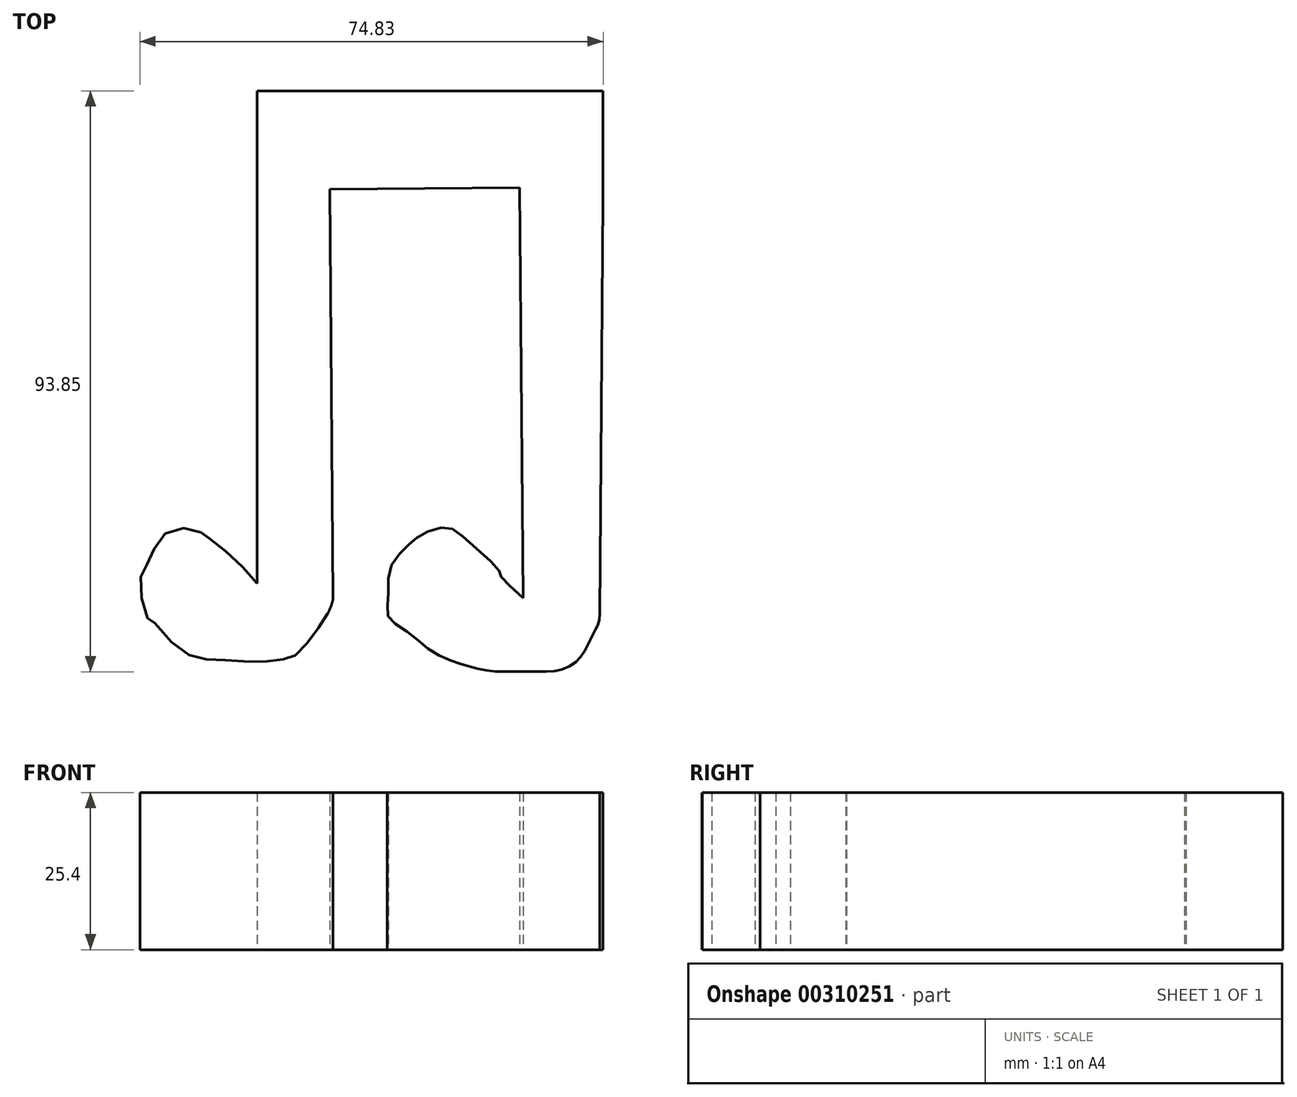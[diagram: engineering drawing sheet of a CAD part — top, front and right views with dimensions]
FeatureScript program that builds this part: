
annotation { "Feature Type Name" : "Feature", "Feature Type Description" : "" }
export const myFeature = defineFeature(function(context is Context, id is Id, definition is map)
    precondition{}
    {
        {
            var Q0;
            Q0=qCreatedBy(makeId("Top.planeOp"),FACE);
            var sketch = newSketch(context, id + "F0", { "sketchPlane" : qUnion([Q0])});
            skLineSegment(sketch, "E0.bottom", {"start": v(-52.73, 52.27) * mm, "end": v(57.91, 52.27) * mm});
            skLineSegment(sketch, "E0.top", {"start": v(-52.73, -55.93) * mm, "end": v(57.91, -55.93) * mm});
            skLineSegment(sketch, "E0.left", {"start": v(-52.73, 52.27) * mm, "end": v(-52.73, -55.93) * mm});
            skLineSegment(sketch, "E0.right", {"start": v(57.91, 52.27) * mm, "end": v(57.91, -55.93) * mm});
            skLineSegment(sketch, "E1", {"start": v(-24.22, 52.27) * mm, "end": v(-24.22, -27.31) * mm});
            skFitSpline(sketch, "E2", {"points": [v(-24.22, -27.31) * mm, v(-28.62, -22.65) * mm, v(-32.5, -19.54) * mm, v(-33.28, -19.03) * mm, v(-37.68, -18.5) * mm, v(-40.79, -21.62) * mm, v(-42.34, -24.98) * mm, v(-43.12, -27.31) * mm, v(-41.82, -33) * mm, v(-41.56, -33) * mm, v(-37.68, -37.15) * mm, v(-33.28, -39.48) * mm, v(-28.88, -39.74) * mm, v(-24.22, -40) * mm, v(-19.56, -39.48) * mm, v(-17.74, -38.7) * mm, v(-14.9, -35.34) * mm, v(-12.82, -32.23) * mm, v(-11.93, -29.64) * mm], "startDerivative": vector(-55.63, 64.73) * mm, "endDerivative": vector(5.4, 55.45) * mm});
            skLineSegment(sketch, "E3", {"start": v(-12.45, 36.38) * mm, "end": v(-11.93, -29.64) * mm});
            skLineSegment(sketch, "E4", {"start": v(-12.45, 36.38) * mm, "end": v(18.24, 36.62) * mm});
            skLineSegment(sketch, "E5", {"start": v(18.24, 36.62) * mm, "end": v(18.76, -29.64) * mm});
            skFitSpline(sketch, "E6", {"points": [v(18.76, -29.64) * mm, v(15.14, -26.02) * mm, v(14.88, -25.24) * mm, v(9.7, -20.32) * mm, v(6.34, -18.25) * mm, v(2.2, -19.54) * mm, v(0, -21.36) * mm, v(-2.73, -24.98) * mm, v(-2.99, -29.64) * mm, v(-2.99, -32.75) * mm, v(0, -35.08) * mm, v(3.49, -37.93) * mm, v(7.11, -39.74) * mm, v(11.25, -41.03) * mm, v(14.88, -41.55) * mm, v(18.76, -41.55) * mm, v(21.87, -41.55) * mm, v(24.72, -41.3) * mm, v(27.3, -40) * mm, v(28.86, -37.93) * mm, v(30.15, -35.34) * mm, v(30.93, -33.78) * mm, v(31.2, -32.23) * mm], "startDerivative": vector(-88.5, 78.58) * mm, "endDerivative": vector(4.73, 52) * mm});
            skFitSpline(sketch, "E7", {"points": [v(-123.12, 34.83) * mm, v(-124.41, 39.49) * mm], "startDerivative": vector(-1.3, 4.66) * mm, "endDerivative": vector(-1.3, 4.66) * mm});
            skLineSegment(sketch, "E8", {"start": v(31.7, 34.57) * mm, "end": v(31.2, -32.23) * mm});
            skLineSegment(sketch, "E9", {"start": v(31.7, 52.27) * mm, "end": v(31.7, 34.57) * mm});
            skLineSegment(sketch, "E10", {"start": v(31.48, 5.57) * mm, "end": v(57.91, 5.57) * mm});
            skLineSegment(sketch, "E11", {"start": v(57.91, -8.93) * mm, "end": v(31.7, -8.73) * mm});
            skLineSegment(sketch, "E12", {"start": v(7.11, -39.74) * mm, "end": v(7.11, -55.93) * mm});
            skLineSegment(sketch, "E13", {"start": v(-12.82, -32.23) * mm, "end": v(-12.82, -58.12) * mm});
            skLineSegment(sketch, "E14", {"start": v(-24.22, 6.35) * mm, "end": v(-52.73, 6.35) * mm});
            skLineSegment(sketch, "E15", {"start": v(-24.47, -7.38) * mm, "end": v(-52.73, -7.38) * mm});
            skLineSegment(sketch, "E16", {"start": v(-12.2, 6.35) * mm, "end": v(18.48, 6.59) * mm});
            skLineSegment(sketch, "E17", {"start": v(18.6, -8.73) * mm, "end": v(-12.1, -8.73) * mm});
            skSolve(sketch);
        }
        {
            var Q0;
            {var subQ1=sQuery(id+"F0.wireOp",EDGE,"E4");Q0=makeQuery(id+"F0.imprint","IMPRINT",FACE,{"disambiguationData":[TD([[makeQuery(id+"F0.imprint","IMPRINT",EDGE,{"derivedFrom":subQ1}),1.0]])]});}
            extrude(context, id + "F1", {"entities" : qUnion([Q0]), "depth" : 25.4 * mm});
        }
    });
